FCSTD DOCUMENT  (FreeCAD 0.17R10665 (Git))
Label: last_april
License: All rights reserved
LicenseURL: http://en.wikipedia.org/wiki/All_rights_reserved
objects: Sketcher::SketchObject×1
note: 1 computed .brp shape members not serialized (recipe doc carries the construction recipe); baked Part::Feature solids carry a one-line shape summary decoded from their .brp

FEATURE [Sketcher::SketchObject] Sketch
  sketch-geometry (34):
    g0: LineSegment StartX=0 StartY=0 StartZ=0 EndX=0 EndY=19 EndZ=0
    g1: LineSegment StartX=0 StartY=19 StartZ=0 EndX=-6.4072 EndY=71.6113 EndZ=0
    g2: LineSegment StartX=-6.4072 StartY=71.6113 StartZ=0 EndX=-125.985 EndY=117.63 EndZ=0
    g3: LineSegment StartX=-125.985 StartY=117.63 StartZ=0 EndX=-146.997 EndY=104.393 EndZ=0
    g4: LineSegment StartX=-146.997 StartY=104.393 StartZ=0 EndX=-164.107 EndY=91.5934 EndZ=0
    g5: LineSegment StartX=-164.107 StartY=91.5934 StartZ=0 EndX=-189.407 EndY=71.6113 EndZ=0
    g6: LineSegment StartX=-189.407 StartY=71.6113 StartZ=0 EndX=-214.059 EndY=53.7081 EndZ=0
    g7: LineSegment StartX=-214.059 StartY=53.7081 StartZ=0 EndX=-236.059 EndY=53.7081 EndZ=0
    g8: LineSegment StartX=-236.059 StartY=53.7081 StartZ=0 EndX=-258.059 EndY=53.7081 EndZ=0
    g9: LineSegment StartX=-156.014 StartY=0 StartZ=0 EndX=-233.014 EndY=0 EndZ=0
    g10: LineSegment StartX=-233.014 StartY=0 StartZ=0 EndX=-211.014 EndY=0 EndZ=0
    g11: LineSegment StartX=-211.014 StartY=0 StartZ=0 EndX=-189.014 EndY=0 EndZ=0
    g12: LineSegment StartX=-189.014 StartY=0 StartZ=0 EndX=-156.014 EndY=0 EndZ=0
    g13: LineSegment StartX=-156.014 StartY=0 StartZ=0 EndX=0 EndY=19 EndZ=0
    g14: LineSegment StartX=-146.997 StartY=104.393 StartZ=0 EndX=-101.418 EndY=6.64898 EndZ=0
    g15: LineSegment StartX=-164.107 StartY=91.5934 StartZ=0 EndX=-123.256 EndY=3.98939 EndZ=0
    g16: LineSegment StartX=-189.407 StartY=71.6113 StartZ=0 EndX=-156.014 EndY=0 EndZ=0
    g17: LineSegment StartX=-6.4072 StartY=71.6113 StartZ=0 EndX=-189.407 EndY=71.6113 EndZ=0
    g18: LineSegment StartX=-214.059 StartY=53.7081 StartZ=0 EndX=-189.014 EndY=0 EndZ=0
    g19: LineSegment StartX=-236.059 StartY=53.7081 StartZ=0 EndX=-211.014 EndY=0 EndZ=0
    g20: LineSegment StartX=-258.059 StartY=53.7081 StartZ=0 EndX=-233.014 EndY=0 EndZ=0
    g21: LineSegment StartX=0 StartY=19 StartZ=0 EndX=-146.997 EndY=104.393 EndZ=0
    g22: LineSegment StartX=0 StartY=19 StartZ=0 EndX=-125.985 EndY=117.63 EndZ=0
    g23: LineSegment StartX=-258.059 StartY=53.7081 StartZ=0 EndX=-275.039 EndY=53.7081 EndZ=0
    g24: LineSegment StartX=0 StartY=19 StartZ=0 EndX=-287.596 EndY=14 EndZ=0
    g25: GeomPoint [constr] X=-263.96 Y=14.4109 Z=0
    g26: LineSegment StartX=-275.039 StartY=53.7081 StartZ=0 EndX=-287.596 EndY=14 EndZ=0
    g27: LineSegment StartX=-287.596 StartY=14 StartZ=0 EndX=-233.014 EndY=0 EndZ=0
    g28: GeomPoint [constr] X=-167.014 Y=0 Z=0
    g29: GeomPoint [constr] X=-145.095 Y=1.3298 Z=0
    g30: LineSegment StartX=-167.014 StartY=0 StartZ=0 EndX=-167.014 EndY=15.5119 EndZ=0
    g31: LineSegment StartX=-145.095 StartY=1.3298 StartZ=0 EndX=-145.095 EndY=17.4735 EndZ=0
    g32: LineSegment StartX=-263.96 StartY=14.4109 StartZ=0 EndX=-263.96 EndY=20.0592 EndZ=0
    g33: LineSegment StartX=0 StartY=0 StartZ=0 EndX=-69.628 EndY=0 EndZ=0
  constraints (84):
    c: Vertical(g0)
    c: Coincident(g0,g1)
    c: Coincident(g1,g2)
    c: Coincident(g2,g3)
    c: Coincident(g3,g4)
    c: Coincident(g4,g5)
    c: Coincident(g5,g6)
    c: Coincident(g6,g7)
    c: Coincident(g7,g8)
    c: Coincident(g9,g10)
    c: Horizontal(g10)
    c: Coincident(g10,g11)
    c: Horizontal(g11)
    c: Coincident(g11,g12)
    c: Coincident(g13,g0)
    c: Distance(g1) = 53
    c: Coincident(g13,g12)
    c: PointOnObject(g12,g-1)
    c: Coincident(g14,g3)
    c: PointOnObject(g14,g13)
    c: Coincident(g15,g4)
    c: PointOnObject(g15,g13)
    c: Coincident(g16,g5)
    c: Coincident(g16,g12)
    c: Perpendicular(g13,g1)
    c: Coincident(g17,g5)
    c: Horizontal(g17)
    c: Angle(g-1,g16) = 2.00713
    c: Parallel(g15,g16)
    c: Parallel(g16,g14)
    c: Coincident(g18,g6)
    c: Coincident(g18,g11)
    c: Coincident(g19,g7)
    c: Coincident(g19,g10)
    c: Coincident(g20,g9)
    c: Parallel(g18,g16)
    c: Parallel(g18,g19)
    c: Parallel(g19,g20)
    c: Coincident(g8,g20)
    c: Distance(g9,g10) = 22
    c: Equal(g10,g11)
    c: Coincident(g17,g1)
    c: Distance(g15,g14) = 22
    c: Distance(g12,g15) = 33
    c: Horizontal(g9)
    c: PointOnObject(g11,g-1)
    c: Distance(g11,g12) = 33
    c: Coincident(g21,g0)
    c: Coincident(g21,g3)
    c: Coincident(g22,g0)
    c: Coincident(g22,g2)
    c: Distance(g22) = 160
    c: Coincident(g8,g23)
    c: Horizontal(g23)
    c: Coincident(g12,g9)
    c: DistanceY(g0,g0) = 19
    c: Coincident(g0,g-1)
    c: Coincident(g24,g0)
    c: DistanceY(g-1,g24) = 14
    c: PointOnObject(g25,g24)
    c: Distance(g25,g0) = 264
    c: Coincident(g23,g26)
    c: Coincident(g26,g24)
    c: Coincident(g26,g27)
    c: Coincident(g27,g9)
    c: Distance(g21) = 170
    c: Parallel(g23,g8)
    c: Parallel(g8,g7)
    c: PointOnObject(g28,g9)
    c: PointOnObject(g29,g13)
    c: DistanceX(g11,g28) = 22
    c: Distance(g29,g15) = 22
    c: Vertical(g31)
    c: Coincident(g32,g25)
    c: Vertical(g32)
    c: Vertical(g30)
    c: Coincident(g31,g29)
    c: Coincident(g33,g-1)
    c: PointOnObject(g33,g-1)
    c: DistanceX(g17,g17) = 183
    c: PointOnObject(g30,g9)
    c: Coincident(g30,g28)
    c: Angle(g22,g13) = 0.785398
    c: Angle(g21,g13) = 0.647459
